# Revit family: 71584-02
name_source: partatom
category: Lighting Fixtures
revit_build: Autodesk Revit 2018 (Build: 20190510_1515(x64)
units: mm (PartAtom-declared; Revit-internal decimal feet)

## family parameters
Always vertical = No
Cut with Voids When Loaded = Yes
Light Source = No
OmniClass Number = 23.80.70.00
OmniClass Title = Lighting
Part Type = Normal
Room Calculation Point = No
Round Connector Dimension = Use Diameter
Shared = No
Work Plane-Based = Yes

## types (2) — shared parameters
Default Elevation = 1219 mm
FARO_Category = Outdoor
FARO_Last Actualization Date = 03/05/2021
FARO_Material_01 = FARO_Metal Dark Grey
FARO_Model Line = SAIGON
FARO_Subcategory = Suspended
Lamp = 1 x E27
Manufacturer = FARO Barcelona
URL = https://www.faro.es
Voltage = 100-240 V

## per-type parameters (varying)
| type | FARO_Description EN | FARO_Description ES | FARO_EAN | FARO_Material_02 | FARO_Ref | FARO_URL Model |
| 71579C-05 SAIGON Grey/matt white pendant lamp T70 cone cap | SAIGON Grey/matt white pendant lamp T70 cone cap | SAIGON Lámpara colgante gris/blanco mate T70 cone cap | 8421776236592 | FARO_Textile_Cream | 71579C-05 | https://faro.es |
| 71584-02 SAIGON Grey portable/pendant lamp R55 | SAIGON Grey portable/pendant lamp R55 | SAIGON Lámpara portátil y colgante gris R55 | https://faro.es | <By Category> | 71584-02 | 8421776236707 |

## geometry (parser evidence)
native form markers: Sweep x13
no freeform markers — native parametric forms only
